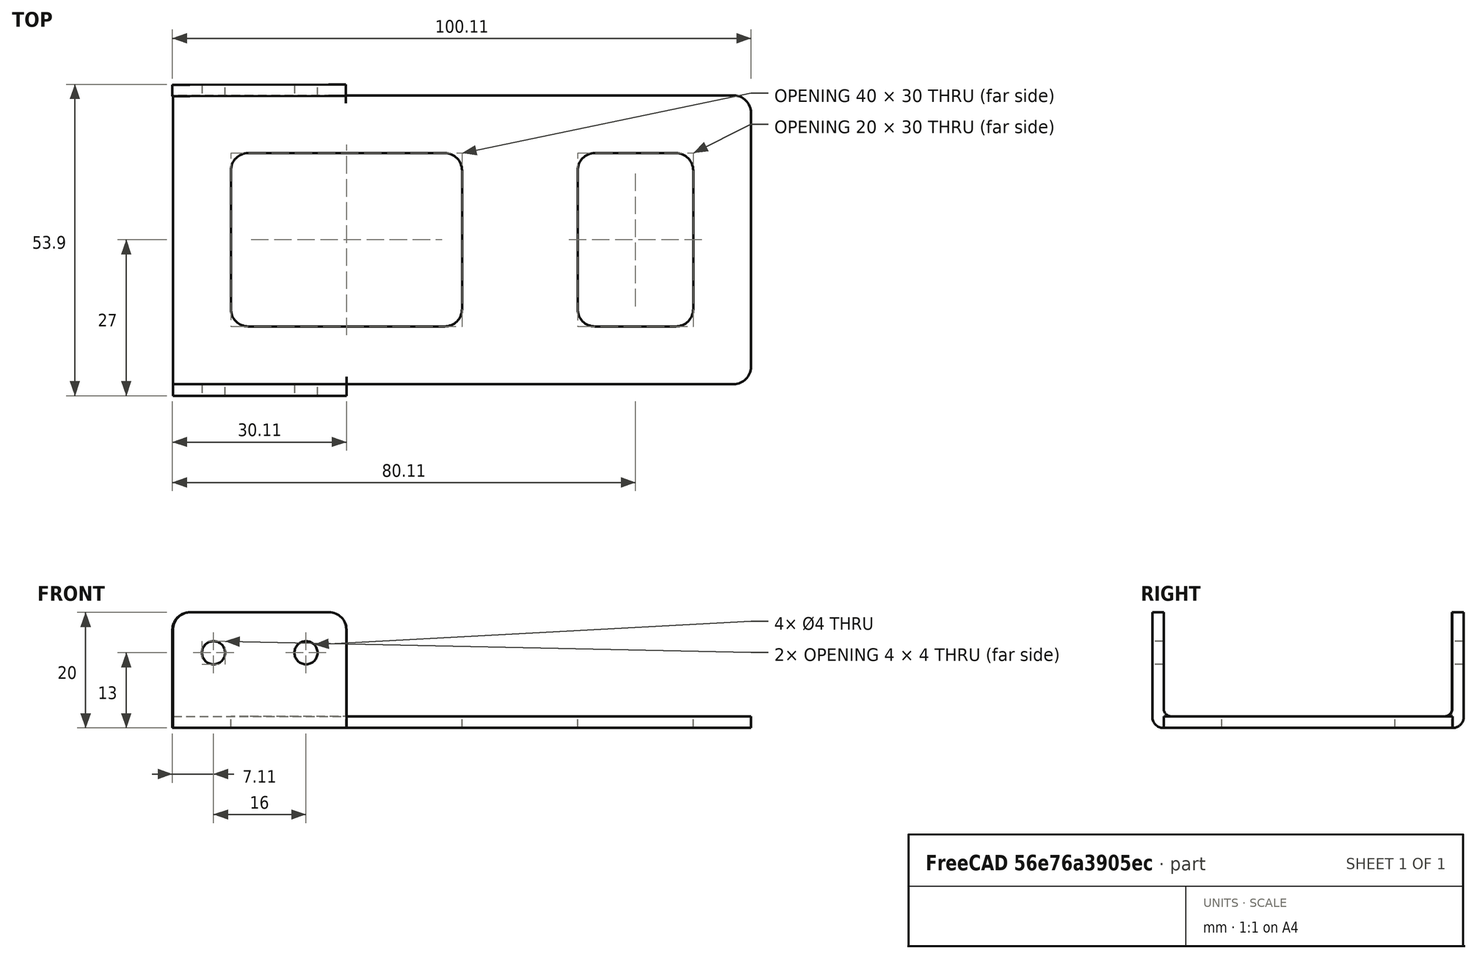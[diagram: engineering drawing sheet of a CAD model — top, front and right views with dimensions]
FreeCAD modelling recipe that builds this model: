
FCSTD DOCUMENT  (FreeCAD 0.21R33771 (Git))
Label: OJT1_T12R03_peça robot
License: All rights reserved
LicenseURL: http://en.wikipedia.org/wiki/All_rights_reserved
objects: Part::Fillet×7, Part::Box×5, Part::MultiFuse×4, Part::Cut×2, Part::Cylinder×2
note: 20 computed .brp shape members not serialized (recipe doc carries the construction recipe); baked Part::Feature solids carry a one-line shape summary decoded from their .brp

FEATURE [Part::Box] Box  label="Cube"
  AttacherType = Attacher::AttachEngine3D
  Height = 2
  Length = 100
  Width = 50
FEATURE [Part::Box] Box001  label="Cube001"
  AttacherType = Attacher::AttachEngine3D
  Height = 10
  Length = 40
  Placement = pos=(10,10,-2) rot=(0,0,1;0rad)
  Width = 30
FEATURE [Part::Box] Box002  label="Cube002"
  AttacherType = Attacher::AttachEngine3D
  Height = 10
  Length = 20
  Placement = pos=(70,10,-2) rot=(0,0,1;0rad)
  Width = 30
FEATURE [Part::MultiFuse] Fusion
  Refine = true
  Shapes = -> [Box002,Box001]
FEATURE [Part::Cut] Cut
  Base = -> Box
  Refine = true
  Tool = -> Fusion
FEATURE [Part::Fillet] Fillet
  Base = -> Cut
  Edges = 8 edges r=3: [Edge29,Edge30,Edge31,Edge32,Edge33,Edge34,Edge35,Edge36]
FEATURE [Part::Fillet] Fillet001
  Base = -> Fillet
  Edges = 2 edges r=3: [Edge41,Edge43]
FEATURE [Part::Box] Box003  label="Cube003"
  AttacherType = Attacher::AttachEngine3D
  Height = 20
  Length = 30
  Placement = pos=(0,-1,2) rot=(0,0,1;0rad)
  Width = 2
FEATURE [Part::Fillet] Fillet002
  Base = -> Box003
  Edges = 1 edges r=1.9: [Edge9]
  Placement = pos=(0,-1,-2) rot=(0,0,1;0rad)
FEATURE [Part::Box] Box004  label="Cube004"
  AttacherType = Attacher::AttachEngine3D
  Height = 20
  Length = 30
  Placement = pos=(0,-1,2) rot=(0,0,1;0rad)
  Width = 2
FEATURE [Part::Fillet] Fillet003
  Base = -> Box004
  Edges = 1 edges r=1.9: [Edge9]
  Placement = pos=(29.8899,50.9038,-2) rot=(0,0,1;3.14334rad)
FEATURE [Part::Fillet] Fillet004
  Base = -> Fillet002
  Edges = 2 edges r=3: [Edge5,Edge12]
FEATURE [Part::Fillet] Fillet005
  Base = -> Fillet003
  Edges = 2 edges r=3: [Edge5,Edge12]
FEATURE [Part::Cylinder] Cylinder
  Angle = 360
  AttacherType = Attacher::AttachEngine3D
  FirstAngle = 0
  Height = 60
  Placement = pos=(7,-6,13) rot=(-1,0,0;1.5708rad)
  Radius = 2
  SecondAngle = 0
FEATURE [Part::Cylinder] Cylinder001
  Angle = 360
  AttacherType = Attacher::AttachEngine3D
  FirstAngle = 0
  Height = 60
  Placement = pos=(23,-6,13) rot=(-1,0,0;1.5708rad)
  Radius = 2
  SecondAngle = 0
FEATURE [Part::MultiFuse] Fusion001
  Refine = true
  Shapes = -> [Fillet005,Fillet004]
FEATURE [Part::MultiFuse] Fusion002
  Refine = true
  Shapes = -> [Cylinder001,Cylinder]
FEATURE [Part::Cut] Cut001
  Base = -> Fusion001
  Refine = true
  Tool = -> Fusion002
FEATURE [Part::MultiFuse] Fusion003
  Refine = true
  Shapes = -> [Fillet001,Cut001]
FEATURE [Part::Fillet] Fillet006
  Base = -> Fusion003
  Edges = 2 edges r=1.25: [Edge2,Edge9]
